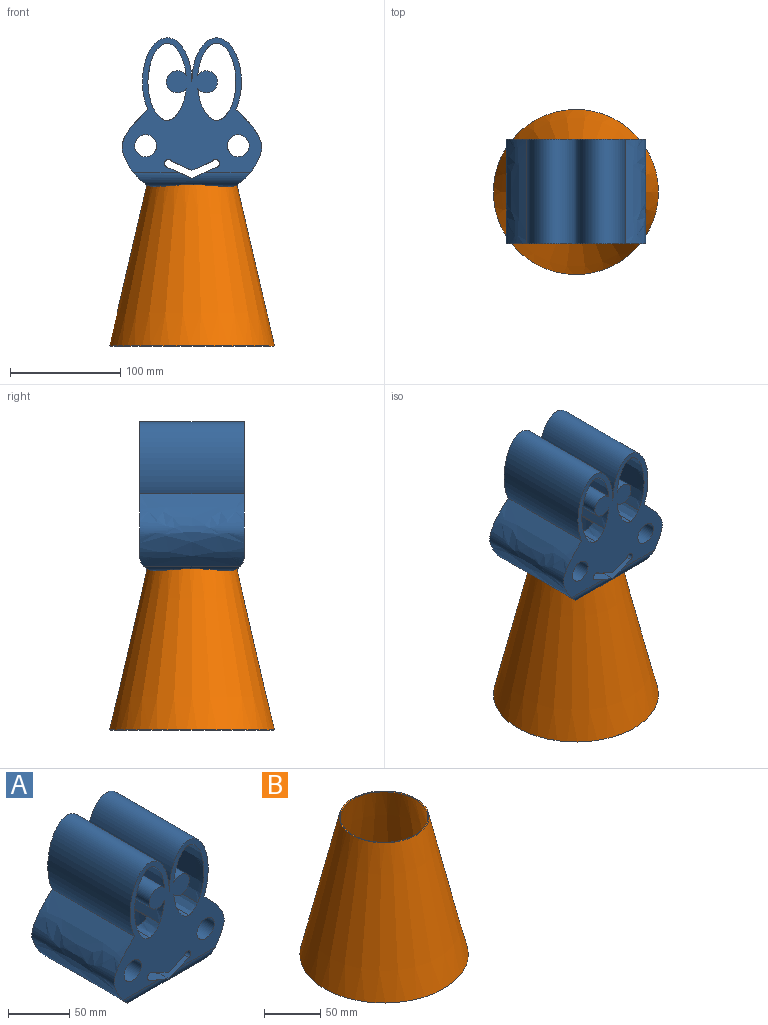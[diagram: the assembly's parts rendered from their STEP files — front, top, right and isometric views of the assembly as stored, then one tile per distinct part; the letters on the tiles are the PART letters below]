
ASSEMBLY  parts=2 mates=1
PART A: 45 faces, bbox 135.4x124.2x135.5 mm
  f0: plane 1.48x1.47mm, normal (0,0,-1), area 1.1mm2, adj f42,f43,f44
  f1: plane 1.48x1.47mm, normal (0,0,-1), area 1.1mm2, adj f41,f42,f44
  f2: plane 1.48x1.47mm, normal (0,0,-1), area 1.1mm2, adj f40,f41,f44
  f3: plane 23.16x21.3mm, normal (-0.4,0,0.91), area 368.9mm2, adj f4,f19,f35,f38,f42,f44
  f4: plane 23.16x21.3mm, normal (0.4,0,0.91), area 368.9mm2, adj f3,f6,f35,f38,f42,f44
  f5: cylinder r=3.72mm len=23.08mm, axis (0,1,0), area 300mm2, adj f7,f22,f34,f38
  f6: cylinder r=3.72mm len=23.08mm, axis (0,1,0), area 300mm2, adj f4,f23,f35,f38
  f7: plane 18.31x17.8mm, normal (-0.4,0,-0.91), area 277.9mm2, adj f5,f8,f34,f38
  f8: plane 18.31x17.8mm, normal (0.4,0,-0.91), area 277.9mm2, adj f7,f20,f34,f38
  f9: extruded ~95x11.34mm, area 528.4mm2, adj f10,f11,f25,f34,f35,f36,f38
  f10: extruded ~35.27x10.29mm, area 356.3mm2, adj f9,f12,f34,f38
  f11: extruded ~35.27x10.29mm, area 356.3mm2, adj f9,f12,f35,f38
  f12: extruded ~95x62.87mm, area 10178.6mm2, adj f10,f11,f32,f34,f35,f37,f38
  f13: extruded ~95x11.34mm, area 528.4mm2, adj f17,f18,f30,f34,f35,f36,f38
  f14: extruded ~95x62.87mm, area 10178.6mm2, adj f17,f18,f31,f34,f35,f38,f39
  f15: cylinder r=10mm len=95mm, axis (0,1,0), area 5620.6mm2, adj f34,f35,f38
  f16: cylinder r=10mm len=95mm, axis (0,1,0), area 5620.6mm2, adj f34,f35,f38
  f17: extruded ~35.27x10.29mm, area 356.3mm2, adj f13,f14,f34,f38
  f18: extruded ~35.27x10.29mm, area 356.3mm2, adj f13,f14,f35,f38
  f19: cylinder r=3.72mm len=23.08mm, axis (0,1,0), area 300mm2, adj f3,f24,f35,f38
  f20: cylinder r=3.72mm len=23.08mm, axis (0,1,0), area 300mm2, adj f8,f21,f34,f38
  f21: plane 23.16x21.3mm, normal (-0.4,0,0.91), area 368.9mm2, adj f20,f22,f34,f38,f40,f44
  f22: plane 23.16x21.3mm, normal (0.4,0,0.91), area 368.9mm2, adj f5,f21,f34,f38,f40,f44
  f23: plane 18.31x17.8mm, normal (-0.4,0,-0.91), area 277.9mm2, adj f6,f24,f35,f38
  f24: plane 18.31x17.8mm, normal (0.4,0,-0.91), area 277.9mm2, adj f19,f23,f35,f38
  f25: extruded ~95x20.1mm, area 2004.1mm2, adj f9,f32,f34,f35
  f26: extruded ~95x65.13mm, area 11963.4mm2, adj f27,f33,f34,f35
  f27: extruded ~95x65.13mm, area 11963.4mm2, adj f26,f28,f34,f35
  f28: extruded ~95x66.73mm, area 7711.9mm2, adj f27,f34,f35,f40,f42,f43
  f29: plane 1.48x1.47mm, normal (0,0,-1), area 1.1mm2, adj f40,f43,f44
  f30: extruded ~95x20.1mm, area 2004.1mm2, adj f13,f31,f34,f35
  f31: cylinder r=10mm len=95mm, axis (0,1,0), area 4719.7mm2, adj f14,f30,f34,f35
  f32: cylinder r=10mm len=95mm, axis (0,1,0), area 4719.7mm2, adj f12,f25,f34,f35
  f33: extruded ~95x66.73mm, area 7711.9mm2, adj f26,f34,f35,f40,f41,f42
  f34: plane 135.07x126.26mm, normal (0,-1,0), area 7346.3mm2, adj f5,f7,f8,f9,f10,f12,f13,f14
  f35: plane 135.07x126.26mm, normal (0,1,0), area 7346.3mm2, adj f3,f4,f6,f9,f11,f12,f13,f14
  f36: plane 70x22.77mm, normal (0,0,-1), area 1565.1mm2, adj f9,f13,f38
  f37: plane 19.48x1.38mm, normal (0,0,-1), area 18mm2, adj f12,f38
  f38: cylinder r=35mm len=70mm, axis (0,0,-1), area 10209.5mm2, adj f3,f4,f5,f6,f7,f8,f9,f10
  f39: plane 19.48x1.38mm, normal (0,0,-1), area 18mm2, adj f14,f38
  f40: cylinder r=13mm len=106.36mm, axis (-1,0,0), area 1424.3mm2, adj f2,f21,f22,f28,f29,f33,f34,f41
  f41: cylinder r=13mm len=86.33mm, axis (0,1,0), area 441.3mm2, adj f1,f2,f33,f40,f42,f44
  f42: cylinder r=13mm len=106.36mm, axis (1,0,0), area 1424.3mm2, adj f0,f1,f3,f4,f28,f33,f35,f41
  f43: cylinder r=13mm len=86.33mm, axis (0,1,0), area 441.3mm2, adj f0,f28,f29,f40,f42,f44
  f44: torus R=48mm, axis (0,0,1), area 3659.1mm2, adj f0,f1,f2,f3,f4,f21,f22,f29
PART B: 4 faces, bbox 150x150x150.2 mm
  f0: cone r=40mm half-angle=76.9deg, axis (0,0,1), area 248.3mm2, adj f2,f3
  f1: cone r=75mm half-angle=76.9deg, axis (0,0,1), area 468.2mm2, adj f2,f3
  f2: cone r=75mm half-angle=13.1deg, axis (0,0,-1), area 55648.2mm2, adj f0,f1
  f3: cone r=74.03mm half-angle=13.1deg, axis (0,0,-1), area 54705.7mm2, adj f0,f1
PLACE A t=(-184.5,3.71,-35.52)mm
PLACE B t=(-184.5,3.71,-30.36)mm fixed
MATE slider B.f0 <-> A.f38  axis (0,0,-1) through (-184.5,3.71,119.41)mm
